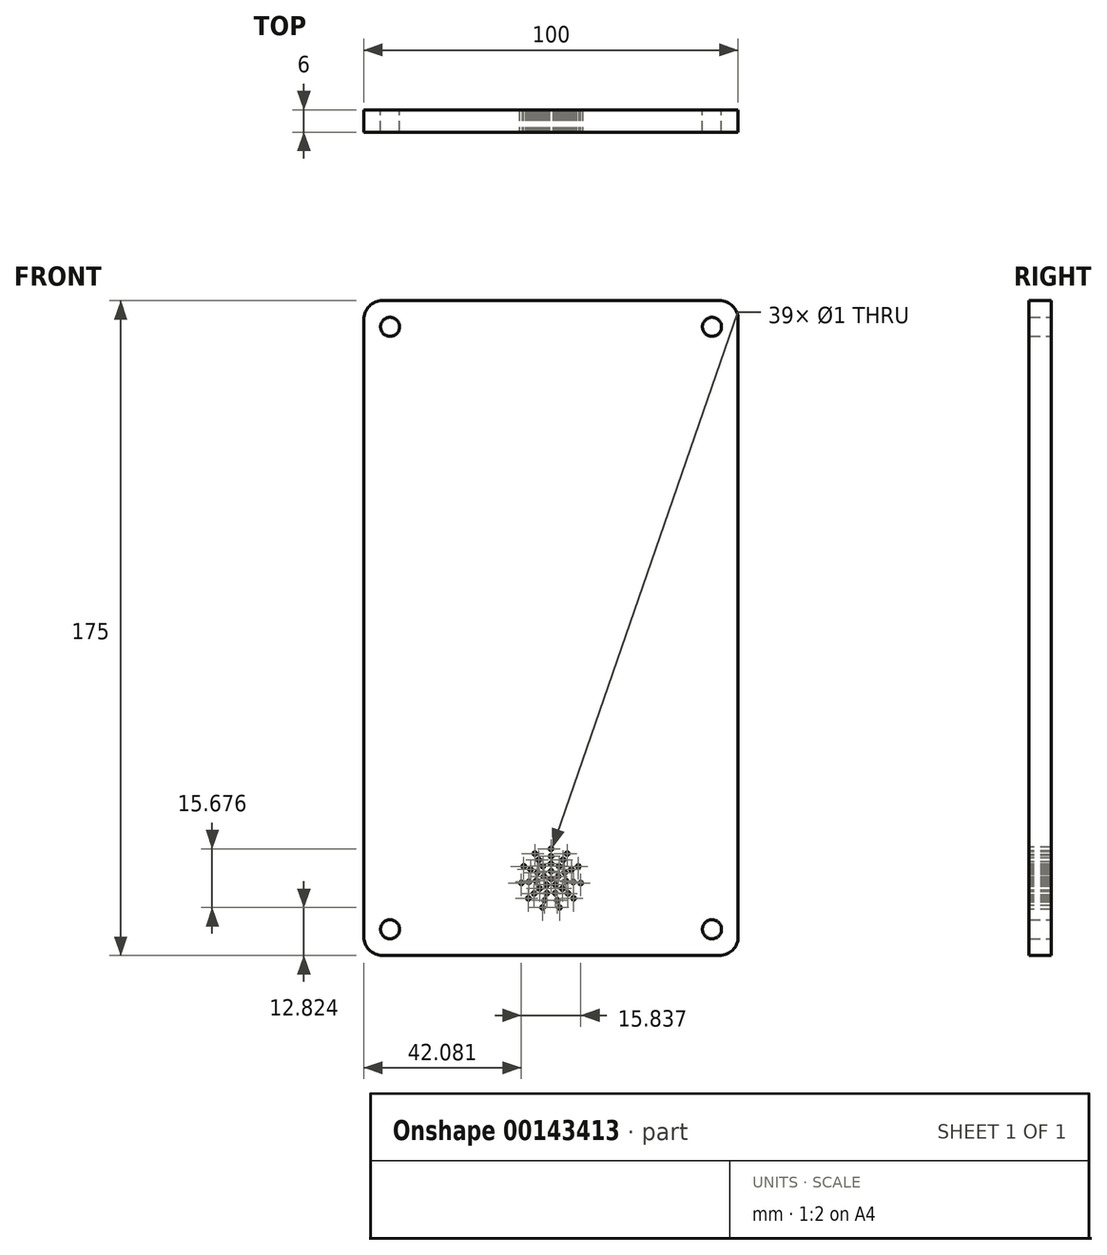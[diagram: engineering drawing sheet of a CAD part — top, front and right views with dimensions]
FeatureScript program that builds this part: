
annotation { "Feature Type Name" : "Feature", "Feature Type Description" : "" }
export const myFeature = defineFeature(function(context is Context, id is Id, definition is map)
    precondition{}
    {
        {
            var Q0;
            Q0=qCreatedBy(makeId("Front.planeOp"),FACE);
            var sketch = newSketch(context, id + "F0", { "sketchPlane" : qUnion([Q0])});
            skLineSegment(sketch, "E0.bottom", {"start": v(50, 87.5) * mm, "end": v(-50, 87.5) * mm});
            skLineSegment(sketch, "E0.top", {"start": v(50, -87.5) * mm, "end": v(-50, -87.5) * mm});
            skLineSegment(sketch, "E0.left", {"start": v(50, 87.5) * mm, "end": v(50, -87.5) * mm});
            skLineSegment(sketch, "E0.right", {"start": v(-50, 87.5) * mm, "end": v(-50, -87.5) * mm});
            skPoint(sketch, "E0.middle", {"position": v(0, 0) * mm});
            skLineSegment(sketch, "E1.bottom", {"start": v(-43, 80.5) * mm, "end": v(43, 80.5) * mm, "construction": true});
            skLineSegment(sketch, "E1.top", {"start": v(-43, -80.5) * mm, "end": v(43, -80.5) * mm, "construction": true});
            skLineSegment(sketch, "E1.left", {"start": v(-43, 80.5) * mm, "end": v(-43, -80.5) * mm, "construction": true});
            skLineSegment(sketch, "E1.right", {"start": v(43, 80.5) * mm, "end": v(43, -80.5) * mm, "construction": true});
            skCircle(sketch, "E2", {"center": v(-43, 80.5) * mm, "radius": 2.55 * mm});
            skCircle(sketch, "E3", {"center": v(43, 80.5) * mm, "radius": 2.55 * mm});
            skCircle(sketch, "E4", {"center": v(43, -80.5) * mm, "radius": 2.55 * mm});
            skCircle(sketch, "E5", {"center": v(-43, -80.5) * mm, "radius": 2.55 * mm});
            skSolve(sketch);
        }
        {
            var Q0;
            Q0=makeQuery(id+"F0.imprint","IMPRINT",FACE,{"disambiguationData":[TD([[makeQuery(id+"F0.imprint","IMPRINT",EDGE,{"derivedFrom":sQuery(id+"F0.wireOp",EDGE,"E0.bottom")}),1.0]])]});
            extrude(context, id + "F1", {"entities" : qUnion([Q0]), "depth" : 6 * mm});
        }
        {
            var Q0;
            Q0=makeQuery(id+"F1.opExtrude","SWEPT_EDGE",EDGE,{"disambiguationData":[OSD([sQuery(id+"F0.wireOp",EDGE,"E0.bottom"),sQuery(id+"F0.wireOp",EDGE,"E0.right")])]});
            var Q1;
            Q1=makeQuery(id+"F1.opExtrude","SWEPT_EDGE",EDGE,{"disambiguationData":[OSD([sQuery(id+"F0.wireOp",EDGE,"E0.top"),sQuery(id+"F0.wireOp",EDGE,"E0.right")])]});
            var Q2;
            Q2=makeQuery(id+"F1.opExtrude","SWEPT_EDGE",EDGE,{"disambiguationData":[OSD([sQuery(id+"F0.wireOp",EDGE,"E0.bottom"),sQuery(id+"F0.wireOp",EDGE,"E0.left")])]});
            var Q3;
            Q3=makeQuery(id+"F1.opExtrude","SWEPT_EDGE",EDGE,{"disambiguationData":[OSD([sQuery(id+"F0.wireOp",EDGE,"E0.top"),sQuery(id+"F0.wireOp",EDGE,"E0.left")])]});
            fillet(context, id + "F2", {"entities" : qUnion([Q0, Q1, Q2, Q3]), "radius" : 5 * mm, "tangentPropagation" : true, "allowEdgeOverflow" : false});
        }
        {
            var Q0;
            Q0=makeQuery(id+"F1.opExtrude","CAP_FACE",FACE,{"disambiguationData":[OSD([sQuery(id+"F0.wireOp",EDGE,"E0.bottom"),sQuery(id+"F0.wireOp",EDGE,"E0.top"),sQuery(id+"F0.wireOp",EDGE,"E0.left"),sQuery(id+"F0.wireOp",EDGE,"E0.right"),sQuery(id+"F0.wireOp",EDGE,"E2"),sQuery(id+"F0.wireOp",EDGE,"E3"),sQuery(id+"F0.wireOp",EDGE,"E4"),sQuery(id+"F0.wireOp",EDGE,"E5")])],"isStart":false});
            var sketch = newSketch(context, id + "F3", { "sketchPlane" : qUnion([Q0])});
            skLineSegment(sketch, "E6", {"start": v(0, -87.5) * mm, "end": v(0, -67) * mm, "construction": true});
            skPoint(sketch, "E6.endSnap0", {"position": v(0, -87.5) * mm});
            skCircle(sketch, "E7", {"center": v(0, -67) * mm, "radius": 0.5 * mm});
            skCircle(sketch, "E8", {"center": v(0, -67) * mm, "radius": 2 * mm, "construction": true});
            skCircle(sketch, "E9", {"center": v(0, -67) * mm, "radius": 4 * mm, "construction": true});
            skCircle(sketch, "E10", {"center": v(0, -67) * mm, "radius": 6 * mm, "construction": true});
            skCircle(sketch, "E11", {"center": v(0, -67) * mm, "radius": 8 * mm, "construction": true});
            skCircle(sketch, "E12", {"center": v(0, -65) * mm, "radius": 0.5 * mm});
            skCircle(sketch, "E13", {"center": v(0, -63) * mm, "radius": 0.5 * mm});
            skCircle(sketch, "E14", {"center": v(0, -61) * mm, "radius": 0.5 * mm});
            skCircle(sketch, "E15", {"center": v(0, -59) * mm, "radius": 0.5 * mm});
            skLineSegment(sketch, "E16.anchor1", {"start": v(0, -67) * mm, "end": v(0, -65) * mm, "construction": true});
            skCircle(sketch, "E17.1.0", {"center": v(-1.9, -66.38) * mm, "radius": 0.5 * mm});
            skCircle(sketch, "E17.2.0", {"center": v(-1.18, -68.62) * mm, "radius": 0.5 * mm});
            skCircle(sketch, "E17.3.0", {"center": v(1.18, -68.62) * mm, "radius": 0.5 * mm});
            skCircle(sketch, "E17.4.0", {"center": v(1.9, -66.38) * mm, "radius": 0.5 * mm});
            skCircle(sketch, "E18.1.0", {"center": v(-2.16, -63.63) * mm, "radius": 0.5 * mm});
            skCircle(sketch, "E18.1.1", {"center": v(-3.24, -61.95) * mm, "radius": 0.5 * mm});
            skCircle(sketch, "E18.1.2", {"center": v(-4.33, -60.27) * mm, "radius": 0.5 * mm});
            skCircle(sketch, "E18.2.0", {"center": v(-3.64, -65.34) * mm, "radius": 0.5 * mm});
            skCircle(sketch, "E18.2.1", {"center": v(-5.46, -64.5) * mm, "radius": 0.5 * mm});
            skCircle(sketch, "E18.2.2", {"center": v(-7.28, -63.68) * mm, "radius": 0.5 * mm});
            skCircle(sketch, "E18.3.0", {"center": v(-3.96, -67.57) * mm, "radius": 0.5 * mm});
            skCircle(sketch, "E18.3.1", {"center": v(-5.94, -67.85) * mm, "radius": 0.5 * mm});
            skCircle(sketch, "E18.3.2", {"center": v(-7.92, -68.14) * mm, "radius": 0.5 * mm});
            skCircle(sketch, "E18.4.0", {"center": v(-3.02, -69.62) * mm, "radius": 0.5 * mm});
            skCircle(sketch, "E18.4.1", {"center": v(-4.53, -70.93) * mm, "radius": 0.5 * mm});
            skCircle(sketch, "E18.4.2", {"center": v(-6.05, -72.24) * mm, "radius": 0.5 * mm});
            skCircle(sketch, "E18.5.0", {"center": v(-1.13, -70.84) * mm, "radius": 0.5 * mm});
            skCircle(sketch, "E18.5.1", {"center": v(-1.7, -72.76) * mm, "radius": 0.5 * mm});
            skCircle(sketch, "E18.5.2", {"center": v(-2.25, -74.68) * mm, "radius": 0.5 * mm});
            skCircle(sketch, "E18.6.0", {"center": v(1.13, -70.84) * mm, "radius": 0.5 * mm});
            skCircle(sketch, "E18.6.1", {"center": v(1.7, -72.76) * mm, "radius": 0.5 * mm});
            skCircle(sketch, "E18.6.2", {"center": v(2.25, -74.68) * mm, "radius": 0.5 * mm});
            skCircle(sketch, "E18.7.0", {"center": v(3.02, -69.62) * mm, "radius": 0.5 * mm});
            skCircle(sketch, "E18.7.1", {"center": v(4.53, -70.93) * mm, "radius": 0.5 * mm});
            skCircle(sketch, "E18.7.2", {"center": v(6.05, -72.24) * mm, "radius": 0.5 * mm});
            skCircle(sketch, "E18.8.0", {"center": v(3.96, -67.57) * mm, "radius": 0.5 * mm});
            skCircle(sketch, "E18.8.1", {"center": v(5.94, -67.85) * mm, "radius": 0.5 * mm});
            skCircle(sketch, "E18.8.2", {"center": v(7.92, -68.14) * mm, "radius": 0.5 * mm});
            skCircle(sketch, "E19.1.9.0", {"center": v(3.64, -65.34) * mm, "radius": 0.5 * mm});
            skCircle(sketch, "E19.2.9.0", {"center": v(5.46, -64.5) * mm, "radius": 0.5 * mm});
            skCircle(sketch, "E19.4.9.0", {"center": v(7.28, -63.68) * mm, "radius": 0.5 * mm});
            skCircle(sketch, "E19.1.10.0", {"center": v(2.16, -63.63) * mm, "radius": 0.5 * mm});
            skCircle(sketch, "E19.2.10.0", {"center": v(3.24, -61.95) * mm, "radius": 0.5 * mm});
            skCircle(sketch, "E19.4.10.0", {"center": v(4.33, -60.27) * mm, "radius": 0.5 * mm});
            skSolve(sketch);
        }
        {
            var Q0;
            Q0 = qSketchRegion(id + "F3", true);
            extrude(context, id + "F4", {"entities" : qUnion([Q0]), "operationType" : NewBodyOperationType.REMOVE, "oppositeDirection" : true, "depth" : 25 * mm});
        }
    });
